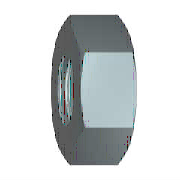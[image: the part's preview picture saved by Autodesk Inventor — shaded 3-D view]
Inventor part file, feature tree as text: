
AUTODESK INVENTOR PART (.ipt)
format: ipt  version: 2024.3 (Build 283343000, 343)  size: 161,792 bytes
history: native  units: mm (DEFAULTED — no unit token found)
features: chamfer x1, hole x1, other x1, plane x1
ambient origin geometry x7: Origin, YZ Plane, XZ Plane, X Axis, Y Axis, Z Axis, Center Point
bodies: Solid1 (feature_tree), Body (feature_tree)
feature tree (4):
  chamfer  "Chamfer1"  Distance=11.547005mm
  hole  "Thread"  [1 undecoded]
  other  "Work Axis1"
  plane  "Work Plane1"
note: 1 required parameter value undecoded (feature->parameter linkage not recoverable at this tier; creation-order binding heuristic only, values carry confidence <= 0.55)
